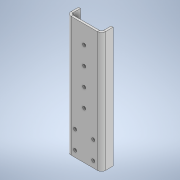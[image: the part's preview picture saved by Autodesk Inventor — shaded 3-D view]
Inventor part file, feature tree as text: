
AUTODESK INVENTOR PART (.ipt)
format: ipt  version: 2022 (Build 260153000, 153)  size: 152,064 bytes
history: native  units: in
note: dims shown in document units (in); Inventor stores cm internally (conversion verified against a paired STEP export)
features: sheet_metal_op x4, sketch x2, other x2, hole x1
ambient origin geometry x8: Origin, YZ Plane, XZ Plane, XY Plane, X Axis, Y Axis, Z Axis, Center Point
bodies: Solid2 (feature_tree)
feature tree (9):
  sketch  "Sketch1"  dims[d0=0.7874in d1=0.7874in]
  sheet_metal_op  "Face1"
  hole  "Hole1"  [1 undecoded]
  sheet_metal_op  "Flange1"
  other  "Plate1"
  sketch  "Sketch2"  dims[d2=0.9843in d3=0.7874in d4=0.2756in d5=0.3543in d6=0.09in d7=0.1339in d8=0.2362in d9=0.2559in d10=0.1181in d11=0.6181in d12=0.09in d13=0.8108in d14=0.09in d15=0.045in d16=0.18in d17=0.09in d18=0.5in d19=90.0deg d20=0.09in d21=0.36in d22=0.09in d23=0.09in]
  other  "Plate2"
  sheet_metal_op  "Bend1"
  sheet_metal_op  "Corner1"
note: 1 required parameter value undecoded (feature->parameter linkage not recoverable at this tier; creation-order binding heuristic only, values carry confidence <= 0.55)
